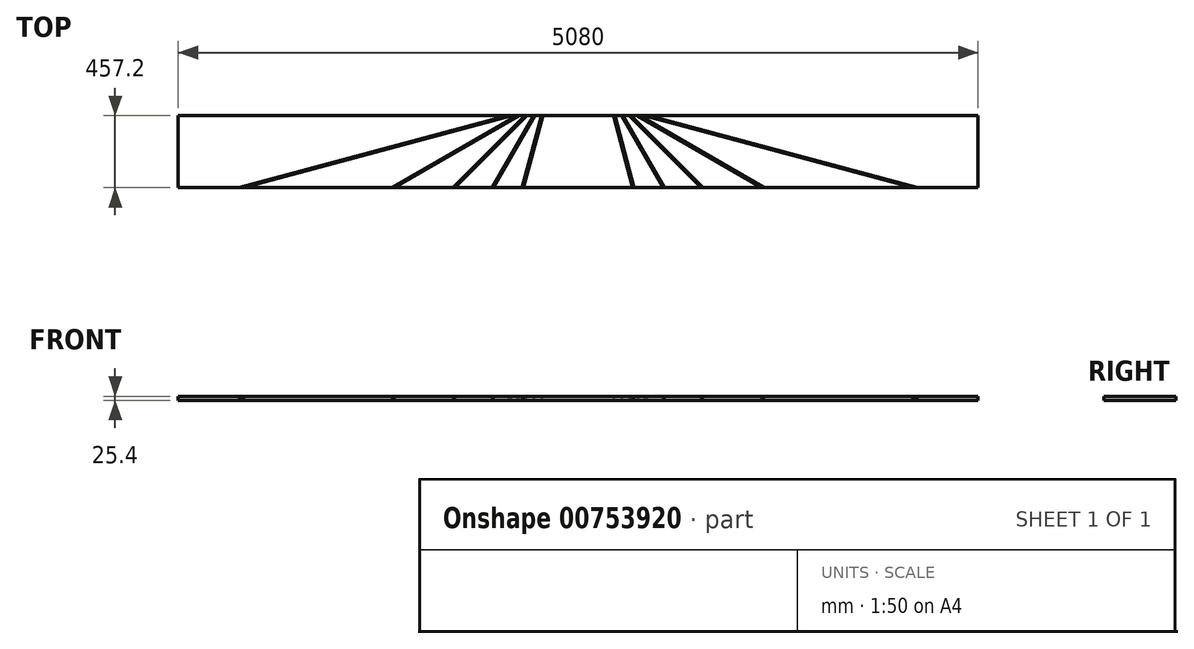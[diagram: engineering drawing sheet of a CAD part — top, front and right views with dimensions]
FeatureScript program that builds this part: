
annotation { "Feature Type Name" : "Feature", "Feature Type Description" : "" }
export const myFeature = defineFeature(function(context is Context, id is Id, definition is map)
    precondition{}
    {
        {
            assignVariable(context, id + "F0", {"name" : "Chamfer", "anyValue" : 9});
        }
        {
            var Q0;
            Q0=qCreatedBy(makeId("Top.planeOp"),FACE);
            var sketch = newSketch(context, id + "F1", { "sketchPlane" : qUnion([Q0])});
            skLineSegment(sketch, "E0.bottom", {"start": v(-2540, 228.6) * mm, "end": v(2540, 228.6) * mm});
            skLineSegment(sketch, "E0.top", {"start": v(-2540, -228.6) * mm, "end": v(2540, -228.6) * mm});
            skLineSegment(sketch, "E0.left", {"start": v(-2540, 228.6) * mm, "end": v(-2540, -228.6) * mm});
            skLineSegment(sketch, "E0.right", {"start": v(2540, 228.6) * mm, "end": v(2540, -228.6) * mm});
            skPoint(sketch, "E0.middle", {"position": v(0, 0) * mm});
            skLineSegment(sketch, "E1", {"start": v(0, 228.6) * mm, "end": v(0, -228.6) * mm, "construction": true});
            skLineSegment(sketch, "E2", {"start": v(-2540, 0) * mm, "end": v(2540, 0) * mm, "construction": true});
            skLineSegment(sketch, "E3", {"start": v(-228.6, 228.6) * mm, "end": v(-351.1, -228.6) * mm});
            skLineSegment(sketch, "E4", {"start": v(-279.4, 228.6) * mm, "end": v(-543.36, -228.6) * mm});
            skLineSegment(sketch, "E5", {"start": v(-330.2, 228.6) * mm, "end": v(-787.4, -228.6) * mm});
            skLineSegment(sketch, "E6", {"start": v(-381, 228.6) * mm, "end": v(-1172.9, -228.6) * mm});
            skLineSegment(sketch, "E7", {"start": v(-431.8, 228.6) * mm, "end": v(-2138.1, -228.6) * mm});
            skPoint(sketch, "E8", {"position": v(-289.85, 0) * mm});
            skPoint(sketch, "E9", {"position": v(-411.38, 0) * mm});
            skPoint(sketch, "E10", {"position": v(-558.8, 0) * mm});
            skPoint(sketch, "E11", {"position": v(-776.95, 0) * mm});
            skPoint(sketch, "E12", {"position": v(-1284.95, 0) * mm});
            skLineSegment(sketch, "E13.MirrorCS", {"start": v(228.6, 228.6) * mm, "end": v(351.1, -228.6) * mm});
            skLineSegment(sketch, "E14.MirrorCS", {"start": v(279.4, 228.6) * mm, "end": v(543.36, -228.6) * mm});
            skLineSegment(sketch, "E15.MirrorCS", {"start": v(330.2, 228.6) * mm, "end": v(787.4, -228.6) * mm});
            skLineSegment(sketch, "E16.MirrorCS", {"start": v(381, 228.6) * mm, "end": v(1172.9, -228.6) * mm});
            skLineSegment(sketch, "E17.MirrorCS", {"start": v(431.8, 228.6) * mm, "end": v(2138.1, -228.6) * mm});
            skSolve(sketch);
        }
        {
            var Q0;
            {var subQ0=sQuery(id+"F1.wireOp",EDGE,"E0.left");Q0=makeQuery(id+"F1.imprint","IMPRINT",FACE,{"disambiguationData":[TD([[makeQuery(id+"F1.imprint","IMPRINT",EDGE,{"derivedFrom":subQ0}),1.0]])]});}
            extrude(context, id + "F2", {"entities" : qUnion([Q0]), "depth" : 25.4 * mm, "offsetDistance" : 25.4 * mm});
        }
        {
            var Q0;
            {var subQ0=sQuery(id+"F1.wireOp",EDGE,"E6");Q0=makeQuery(id+"F1.imprint","IMPRINT",FACE,{"disambiguationData":[TD([[makeQuery(id+"F1.imprint","IMPRINT",EDGE,{"derivedFrom":subQ0}),-1.0]])]});}
            extrude(context, id + "F3", {"entities" : qUnion([Q0]), "depth" : 25.4 * mm, "offsetDistance" : 25.4 * mm});
        }
        {
            var Q0;
            {var subQ0=sQuery(id+"F1.wireOp",EDGE,"E5");Q0=makeQuery(id+"F1.imprint","IMPRINT",FACE,{"disambiguationData":[TD([[makeQuery(id+"F1.imprint","IMPRINT",EDGE,{"derivedFrom":subQ0}),-1.0]])]});}
            extrude(context, id + "F4", {"entities" : qUnion([Q0]), "depth" : 25.4 * mm, "offsetDistance" : 25.4 * mm});
        }
        {
            var Q0;
            {var subQ0=sQuery(id+"F1.wireOp",EDGE,"E4");Q0=makeQuery(id+"F1.imprint","IMPRINT",FACE,{"disambiguationData":[TD([[makeQuery(id+"F1.imprint","IMPRINT",EDGE,{"derivedFrom":subQ0}),-1.0]])]});}
            extrude(context, id + "F5", {"entities" : qUnion([Q0]), "depth" : 25.4 * mm, "offsetDistance" : 25.4 * mm});
        }
        {
            var Q0;
            {var subQ0=sQuery(id+"F1.wireOp",EDGE,"E3");Q0=makeQuery(id+"F1.imprint","IMPRINT",FACE,{"disambiguationData":[TD([[makeQuery(id+"F1.imprint","IMPRINT",EDGE,{"derivedFrom":subQ0}),-1.0]])]});}
            extrude(context, id + "F6", {"entities" : qUnion([Q0]), "depth" : 25.4 * mm, "offsetDistance" : 25.4 * mm});
        }
        {
            var Q0;
            {var subQ0=sQuery(id+"F1.wireOp",EDGE,"E3");Q0=makeQuery(id+"F1.imprint","IMPRINT",FACE,{"disambiguationData":[TD([[makeQuery(id+"F1.imprint","IMPRINT",EDGE,{"derivedFrom":subQ0}),1.0]])]});}
            extrude(context, id + "F7", {"entities" : qUnion([Q0]), "depth" : 25.4 * mm, "offsetDistance" : 25.4 * mm});
        }
        {
            var Q0;
            {var subQ0=sQuery(id+"F1.wireOp",EDGE,"E13.MirrorCS");Q0=makeQuery(id+"F1.imprint","IMPRINT",FACE,{"disambiguationData":[TD([[makeQuery(id+"F1.imprint","IMPRINT",EDGE,{"derivedFrom":subQ0}),1.0]])]});}
            extrude(context, id + "F8", {"entities" : qUnion([Q0]), "depth" : 25.4 * mm, "offsetDistance" : 25.4 * mm});
        }
        {
            var Q0;
            {var subQ0=sQuery(id+"F1.wireOp",EDGE,"E14.MirrorCS");Q0=makeQuery(id+"F1.imprint","IMPRINT",FACE,{"disambiguationData":[TD([[makeQuery(id+"F1.imprint","IMPRINT",EDGE,{"derivedFrom":subQ0}),1.0]])]});}
            extrude(context, id + "F9", {"entities" : qUnion([Q0]), "depth" : 25.4 * mm, "offsetDistance" : 25.4 * mm});
        }
        {
            var Q0;
            {var subQ0=sQuery(id+"F1.wireOp",EDGE,"E15.MirrorCS");Q0=makeQuery(id+"F1.imprint","IMPRINT",FACE,{"disambiguationData":[TD([[makeQuery(id+"F1.imprint","IMPRINT",EDGE,{"derivedFrom":subQ0}),1.0]])]});}
            extrude(context, id + "F10", {"entities" : qUnion([Q0]), "depth" : 25.4 * mm, "offsetDistance" : 25.4 * mm});
        }
        {
            var Q0;
            {var subQ0=sQuery(id+"F1.wireOp",EDGE,"E16.MirrorCS");Q0=makeQuery(id+"F1.imprint","IMPRINT",FACE,{"disambiguationData":[TD([[makeQuery(id+"F1.imprint","IMPRINT",EDGE,{"derivedFrom":subQ0}),1.0]])]});}
            extrude(context, id + "F11", {"entities" : qUnion([Q0]), "depth" : 25.4 * mm, "offsetDistance" : 25.4 * mm});
        }
        {
            var Q0;
            {var subQ0=sQuery(id+"F1.wireOp",EDGE,"E0.right");Q0=makeQuery(id+"F1.imprint","IMPRINT",FACE,{"disambiguationData":[TD([[makeQuery(id+"F1.imprint","IMPRINT",EDGE,{"derivedFrom":subQ0}),-1.0]])]});}
            extrude(context, id + "F12", {"entities" : qUnion([Q0]), "depth" : 25.4 * mm, "offsetDistance" : 25.4 * mm});
        }
        {
            var Q0;
            Q0=makeQuery(id+"F2.opExtrude","CAP_EDGE",EDGE,{"disambiguationData":[OSD([sQuery(id+"F1.wireOp",EDGE,"E7")])],"isStart":false});
            chamfer(context, id + "F13", {"entities" : qUnion([Q0]), "chamferType" : ChamferType.OFFSET_ANGLE, "width" : 25.4 * mm, "oppositeDirection" : false, "angle" : (getVariable(context, 'Chamfer')) * degree, "tangentPropagation" : true});
        }
        {
            var Q0;
            Q0=makeQuery(id+"F3.opExtrude","CAP_EDGE",EDGE,{"disambiguationData":[OSD([sQuery(id+"F1.wireOp",EDGE,"E7")])],"isStart":false});
            var Q1;
            Q1=makeQuery(id+"F3.opExtrude","CAP_EDGE",EDGE,{"disambiguationData":[OSD([sQuery(id+"F1.wireOp",EDGE,"E6")])],"isStart":false});
            chamfer(context, id + "F14", {"entities" : qUnion([Q0, Q1]), "chamferType" : ChamferType.OFFSET_ANGLE, "width" : 25.4 * mm, "oppositeDirection" : true, "angle" : (getVariable(context, 'Chamfer')) * degree, "tangentPropagation" : true});
        }
        {
            var Q0;
            Q0=makeQuery(id+"F4.opExtrude","CAP_EDGE",EDGE,{"disambiguationData":[OSD([sQuery(id+"F1.wireOp",EDGE,"E6")])],"isStart":false});
            var Q1;
            Q1=makeQuery(id+"F4.opExtrude","CAP_EDGE",EDGE,{"disambiguationData":[OSD([sQuery(id+"F1.wireOp",EDGE,"E5")])],"isStart":false});
            chamfer(context, id + "F15", {"entities" : qUnion([Q0, Q1]), "chamferType" : ChamferType.OFFSET_ANGLE, "width" : 25.4 * mm, "oppositeDirection" : true, "angle" : (getVariable(context, 'Chamfer')) * degree, "tangentPropagation" : true});
        }
        {
            var Q0;
            Q0=makeQuery(id+"F5.opExtrude","CAP_EDGE",EDGE,{"disambiguationData":[OSD([sQuery(id+"F1.wireOp",EDGE,"E5")])],"isStart":false});
            var Q1;
            Q1=makeQuery(id+"F5.opExtrude","CAP_EDGE",EDGE,{"disambiguationData":[OSD([sQuery(id+"F1.wireOp",EDGE,"E4")])],"isStart":false});
            chamfer(context, id + "F16", {"entities" : qUnion([Q0, Q1]), "chamferType" : ChamferType.OFFSET_ANGLE, "width" : 25.4 * mm, "oppositeDirection" : true, "angle" : (getVariable(context, 'Chamfer')) * degree, "tangentPropagation" : true});
        }
        {
            var Q0;
            Q0=makeQuery(id+"F6.opExtrude","CAP_EDGE",EDGE,{"disambiguationData":[OSD([sQuery(id+"F1.wireOp",EDGE,"E4")])],"isStart":false});
            var Q1;
            Q1=makeQuery(id+"F6.opExtrude","CAP_EDGE",EDGE,{"disambiguationData":[OSD([sQuery(id+"F1.wireOp",EDGE,"E3")])],"isStart":false});
            chamfer(context, id + "F17", {"entities" : qUnion([Q0, Q1]), "chamferType" : ChamferType.OFFSET_ANGLE, "width" : 25.4 * mm, "oppositeDirection" : true, "angle" : (getVariable(context, 'Chamfer')) * degree, "tangentPropagation" : true});
        }
        {
            var Q0;
            Q0=makeQuery(id+"F7.opExtrude","CAP_EDGE",EDGE,{"disambiguationData":[OSD([sQuery(id+"F1.wireOp",EDGE,"E3")])],"isStart":false});
            var Q1;
            Q1=makeQuery(id+"F7.opExtrude","CAP_EDGE",EDGE,{"disambiguationData":[OSD([sQuery(id+"F1.wireOp",EDGE,"E13.MirrorCS")])],"isStart":false});
            chamfer(context, id + "F18", {"entities" : qUnion([Q0, Q1]), "chamferType" : ChamferType.OFFSET_ANGLE, "width" : 25.4 * mm, "oppositeDirection" : true, "angle" : (getVariable(context, 'Chamfer')) * degree, "tangentPropagation" : true});
        }
        {
            var Q0;
            Q0=makeQuery(id+"F8.opExtrude","CAP_EDGE",EDGE,{"disambiguationData":[OSD([sQuery(id+"F1.wireOp",EDGE,"E13.MirrorCS")])],"isStart":false});
            var Q1;
            Q1=makeQuery(id+"F8.opExtrude","CAP_EDGE",EDGE,{"disambiguationData":[OSD([sQuery(id+"F1.wireOp",EDGE,"E14.MirrorCS")])],"isStart":false});
            chamfer(context, id + "F19", {"entities" : qUnion([Q0, Q1]), "chamferType" : ChamferType.OFFSET_ANGLE, "width" : 25.4 * mm, "oppositeDirection" : true, "angle" : (getVariable(context, 'Chamfer')) * degree, "tangentPropagation" : true});
        }
        {
            var Q0;
            Q0=makeQuery(id+"F9.opExtrude","CAP_EDGE",EDGE,{"disambiguationData":[OSD([sQuery(id+"F1.wireOp",EDGE,"E14.MirrorCS")])],"isStart":false});
            var Q1;
            Q1=makeQuery(id+"F9.opExtrude","CAP_EDGE",EDGE,{"disambiguationData":[OSD([sQuery(id+"F1.wireOp",EDGE,"E15.MirrorCS")])],"isStart":false});
            chamfer(context, id + "F20", {"entities" : qUnion([Q0, Q1]), "chamferType" : ChamferType.OFFSET_ANGLE, "width" : 25.4 * mm, "oppositeDirection" : true, "angle" : (getVariable(context, 'Chamfer')) * degree, "tangentPropagation" : true});
        }
        {
            var Q0;
            Q0=makeQuery(id+"F10.opExtrude","CAP_EDGE",EDGE,{"disambiguationData":[OSD([sQuery(id+"F1.wireOp",EDGE,"E15.MirrorCS")])],"isStart":false});
            var Q1;
            Q1=makeQuery(id+"F10.opExtrude","CAP_EDGE",EDGE,{"disambiguationData":[OSD([sQuery(id+"F1.wireOp",EDGE,"E16.MirrorCS")])],"isStart":false});
            chamfer(context, id + "F21", {"entities" : qUnion([Q0, Q1]), "chamferType" : ChamferType.OFFSET_ANGLE, "width" : 25.4 * mm, "oppositeDirection" : true, "angle" : (getVariable(context, 'Chamfer')) * degree, "tangentPropagation" : true});
        }
        {
            var Q0;
            Q0=makeQuery(id+"F11.opExtrude","CAP_EDGE",EDGE,{"disambiguationData":[OSD([sQuery(id+"F1.wireOp",EDGE,"E16.MirrorCS")])],"isStart":false});
            var Q1;
            Q1=makeQuery(id+"F11.opExtrude","CAP_EDGE",EDGE,{"disambiguationData":[OSD([sQuery(id+"F1.wireOp",EDGE,"E17.MirrorCS")])],"isStart":false});
            chamfer(context, id + "F22", {"entities" : qUnion([Q0, Q1]), "chamferType" : ChamferType.OFFSET_ANGLE, "width" : 25.4 * mm, "oppositeDirection" : true, "angle" : (getVariable(context, 'Chamfer')) * degree, "tangentPropagation" : true});
        }
        {
            var Q0;
            Q0=makeQuery(id+"F12.opExtrude","CAP_EDGE",EDGE,{"disambiguationData":[OSD([sQuery(id+"F1.wireOp",EDGE,"E17.MirrorCS")])],"isStart":false});
            chamfer(context, id + "F23", {"entities" : qUnion([Q0]), "chamferType" : ChamferType.OFFSET_ANGLE, "width" : 25.4 * mm, "oppositeDirection" : true, "angle" : (getVariable(context, 'Chamfer')) * degree, "tangentPropagation" : true});
        }
    });
